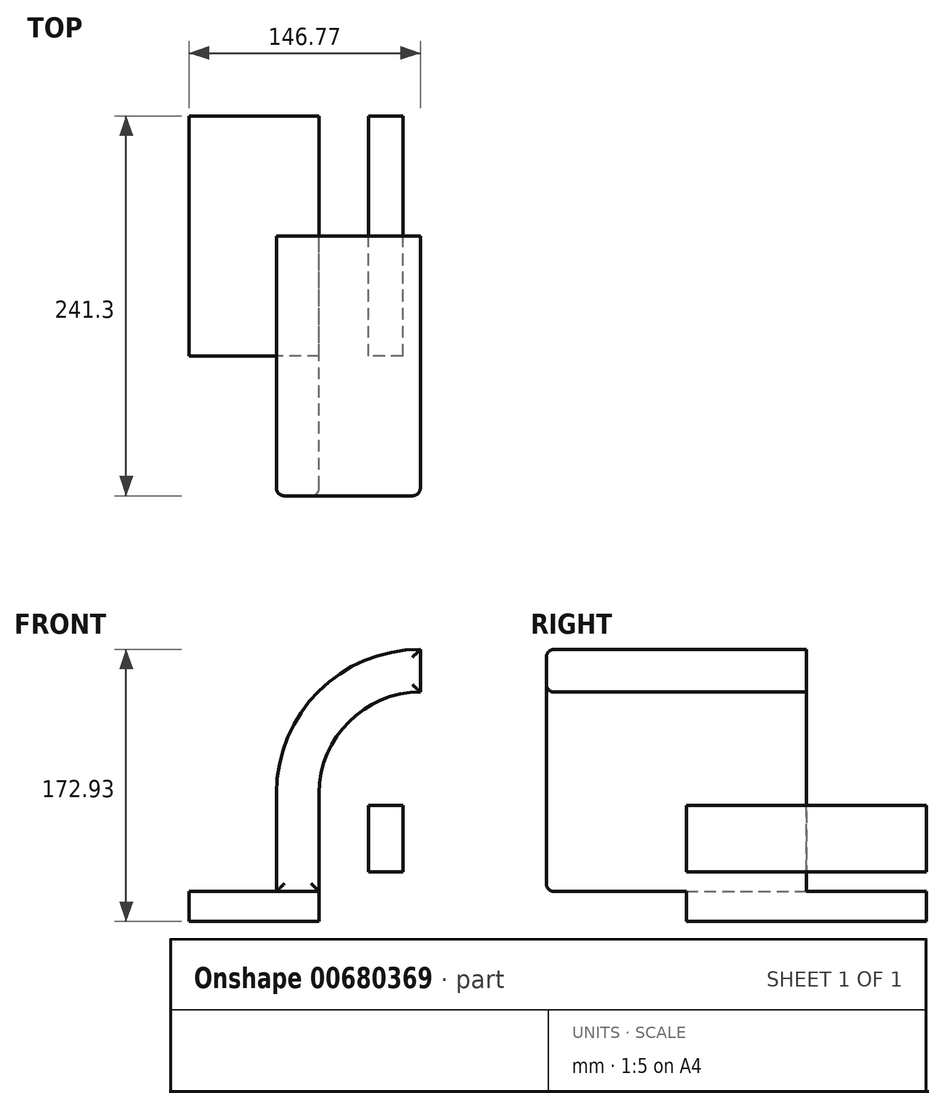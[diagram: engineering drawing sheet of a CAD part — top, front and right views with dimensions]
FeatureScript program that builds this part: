
annotation { "Feature Type Name" : "Feature", "Feature Type Description" : "" }
export const myFeature = defineFeature(function(context is Context, id is Id, definition is map)
    precondition{}
    {
        {
            var Q0;
            Q0=qCreatedBy(makeId("Front.planeOp"),FACE);
            var sketch = newSketch(context, id + "F0", { "sketchPlane" : qUnion([Q0])});
            skLineSegment(sketch, "E0.bottom", {"start": v(41.27, 9.53) * mm, "end": v(-41.28, 9.53) * mm});
            skLineSegment(sketch, "E0.top", {"start": v(41.27, -9.52) * mm, "end": v(-41.28, -9.52) * mm});
            skLineSegment(sketch, "E0.left", {"start": v(41.27, 9.53) * mm, "end": v(41.27, -9.52) * mm});
            skLineSegment(sketch, "E0.right", {"start": v(-41.28, 9.52) * mm, "end": v(-41.28, -9.52) * mm});
            skPoint(sketch, "E0.middle", {"position": v(0, 0) * mm});
            skLineSegment(sketch, "E1.bottom", {"start": v(94.54, 22.08) * mm, "end": v(72.64, 22.08) * mm});
            skLineSegment(sketch, "E1.top", {"start": v(94.54, 64.39) * mm, "end": v(72.64, 64.39) * mm});
            skLineSegment(sketch, "E1.left", {"start": v(94.54, 22.08) * mm, "end": v(94.54, 64.39) * mm});
            skLineSegment(sketch, "E1.right", {"start": v(72.64, 22.08) * mm, "end": v(72.64, 64.39) * mm});
            skPoint(sketch, "E1.middle", {"position": v(83.59, 43.23) * mm});
            skLineSegment(sketch, "E2", {"start": v(41.27, 9.53) * mm, "end": v(41.27, 72) * mm});
            skArc(sketch, "E3", {"start": v(41.27, 72) * mm, "mid": v(60.08, 117.41) * mm, "end": v(105.49, 136.22) * mm});
            skLineSegment(sketch, "E4", {"start": v(83.59, 136.22) * mm, "end": v(105.49, 136.22) * mm});
            skPoint(sketch, "E4.endSnap0", {"position": v(83.59, 64.39) * mm});
            skArc(sketch, "E5.0", {"start": v(14.1, 72) * mm, "mid": v(40.86, 136.63) * mm, "end": v(105.49, 163.4) * mm});
            skLineSegment(sketch, "E6", {"start": v(105.49, 163.4) * mm, "end": v(105.49, 136.22) * mm});
            skLineSegment(sketch, "E7", {"start": v(14.1, 72) * mm, "end": v(14.1, 9.53) * mm});
            skSolve(sketch);
        }
        {
            var Q0;
            Q0=makeQuery(id+"F0.imprint","IMPRINT",FACE,{"disambiguationData":[TD([[makeQuery(id+"F0.imprint","IMPRINT",EDGE,{"derivedFrom":sQuery(id+"F0.wireOp",EDGE,"E0.top")}),-1.0]])]});
            var Q1;
            Q1=makeQuery(id+"F0.imprint","IMPRINT",FACE,{"disambiguationData":[TD([[makeQuery(id+"F0.imprint","IMPRINT",EDGE,{"derivedFrom":sQuery(id+"F0.wireOp",EDGE,"E1.bottom")}),-1.0]])]});
            extrude(context, id + "F1", {"entities" : qUnion([Q0, Q1]), "endBound" : BoundingType.SYMMETRIC, "depth" : 152.4 * mm, "offsetDistance" : 25.4 * mm});
        }
        {
            var Q0;
            {var subQ0=sQuery(id+"F0.wireOp",EDGE,"E2");Q0=makeQuery(id+"F0.imprint","IMPRINT",FACE,{"disambiguationData":[TD([[makeQuery(id+"F0.imprint","IMPRINT",EDGE,{"derivedFrom":subQ0}),1.0]])]});}
            extrude(context, id + "F2", {"entities" : qUnion([Q0]), "operationType" : NewBodyOperationType.ADD, "depth" : 165.1 * mm, "offsetDistance" : 25.4 * mm});
        }
        {
            var Q0;
            Q0=makeQuery(id+"F2.opExtrude","CAP_EDGE",EDGE,{"disambiguationData":[OSD([sQuery(id+"F0.wireOp",EDGE,"E2")])],"isStart":false});
            var Q1;
            Q1=makeQuery(id+"F2.opExtrude","CAP_FACE",FACE,{"disambiguationData":[OSD([sQuery(id+"F0.wireOp",EDGE,"E0.bottom"),sQuery(id+"F0.wireOp",EDGE,"E2"),sQuery(id+"F0.wireOp",EDGE,"E3"),sQuery(id+"F0.wireOp",EDGE,"E5.0"),sQuery(id+"F0.wireOp",EDGE,"E6"),sQuery(id+"F0.wireOp",EDGE,"E7")])],"isStart":false});
            fillet(context, id + "F3", {"entities" : qUnion([Q0, Q1]), "radius" : 5.08 * mm, "tangentPropagation" : true, "allowEdgeOverflow" : false});
        }
    });
